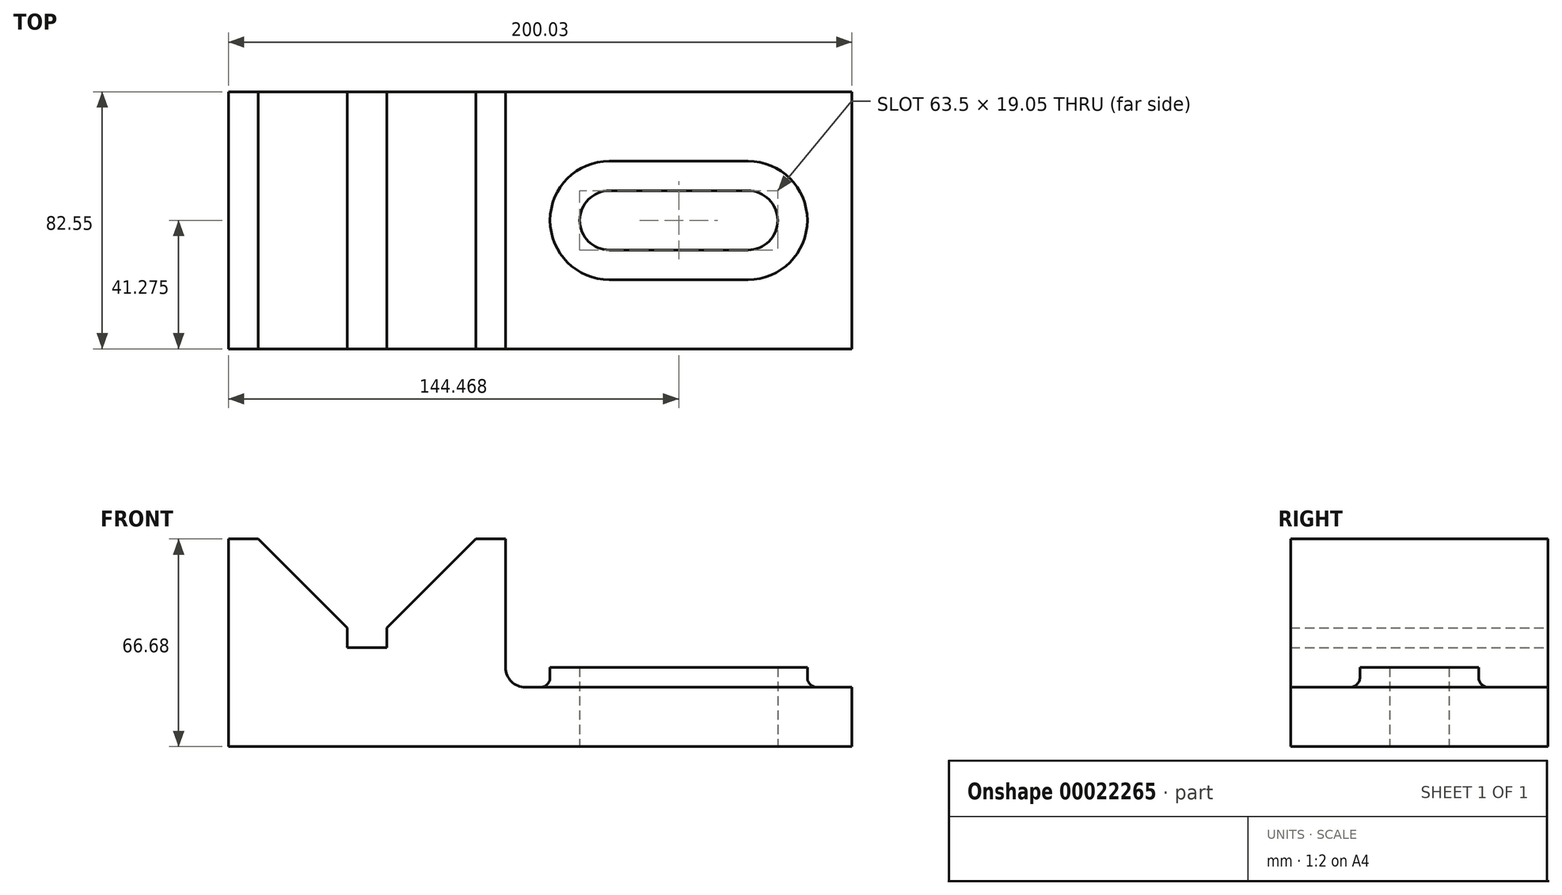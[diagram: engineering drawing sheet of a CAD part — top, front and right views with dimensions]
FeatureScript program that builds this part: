
annotation { "Feature Type Name" : "Feature", "Feature Type Description" : "" }
export const myFeature = defineFeature(function(context is Context, id is Id, definition is map)
    precondition{}
    {
        {
            var Q0;
            Q0=qCreatedBy(makeId("Front.planeOp"),FACE);
            var sketch = newSketch(context, id + "F0", { "sketchPlane" : qUnion([Q0])});
            skLineSegment(sketch, "E0.bottom", {"start": v(0, 0) * mm, "end": v(-200.03, 0) * mm});
            skLineSegment(sketch, "E0.top", {"start": v(0, 66.68) * mm, "end": v(-200.03, 66.68) * mm});
            skLineSegment(sketch, "E0.left", {"start": v(0, 0) * mm, "end": v(0, 66.68) * mm});
            skLineSegment(sketch, "E0.right", {"start": v(-200.03, 0) * mm, "end": v(-200.03, 66.67) * mm});
            skLineSegment(sketch, "E1", {"start": v(-190.5, 66.67) * mm, "end": v(-161.92, 38.1) * mm});
            skLineSegment(sketch, "E2", {"start": v(-161.92, 38.1) * mm, "end": v(-161.92, 31.75) * mm});
            skLineSegment(sketch, "E3", {"start": v(-161.92, 31.75) * mm, "end": v(-149.22, 31.75) * mm});
            skLineSegment(sketch, "E4", {"start": v(-149.22, 31.75) * mm, "end": v(-149.22, 38.1) * mm});
            skLineSegment(sketch, "E5", {"start": v(-149.22, 38.1) * mm, "end": v(-120.65, 66.67) * mm});
            skLineSegment(sketch, "E6", {"start": v(-111.12, 66.67) * mm, "end": v(-111.12, 0) * mm});
            skLineSegment(sketch, "E7", {"start": v(-161.92, 38.1) * mm, "end": v(-186.95, 38.1) * mm, "construction": true});
            skLineSegment(sketch, "E8", {"start": v(-149.22, 38.1) * mm, "end": v(-132.28, 38.1) * mm, "construction": true});
            skLineSegment(sketch, "E9", {"start": v(-111.12, 19.05) * mm, "end": v(0, 19.05) * mm});
            skSolve(sketch);
        }
        {
            var Q0;
            {var subQ0=sQuery(id+"F0.wireOp",EDGE,"E9");Q0=makeQuery(id+"F0.imprint","IMPRINT",FACE,{"disambiguationData":[TD([[makeQuery(id+"F0.imprint","IMPRINT",EDGE,{"derivedFrom":subQ0}),-1.0]])]});}
            var Q1;
            {var subQ8=sQuery(id+"F0.wireOp",EDGE,"E0.right");Q1=makeQuery(id+"F0.imprint","IMPRINT",FACE,{"disambiguationData":[TD([[makeQuery(id+"F0.imprint","IMPRINT",EDGE,{"derivedFrom":subQ8}),-1.0]])]});}
            extrude(context, id + "F1", {"entities" : qUnion([Q0, Q1]), "depth" : 82.55 * mm});
        }
        {
            var Q0;
            Q0=makeQuery(id+"F1.opExtrude","SWEPT_FACE",FACE,{"disambiguationData":[OSD([sQuery(id+"F0.wireOp",EDGE,"E9")])]});
            var sketch = newSketch(context, id + "F2", { "sketchPlane" : qUnion([Q0])});
            skLineSegment(sketch, "E10", {"start": v(0, -41.28) * mm, "end": v(-111.12, -41.28) * mm, "construction": true});
            skLineSegment(sketch, "E11", {"start": v(-55.56, -41.28) * mm, "end": v(-55.56, -2.33) * mm, "construction": true});
            skLineSegment(sketch, "E12", {"start": v(-55.56, -41.28) * mm, "end": v(-55.56, -63.94) * mm, "construction": true});
            skCircle(sketch, "E13", {"center": v(-77.79, -41.28) * mm, "radius": 9.53 * mm});
            skCircle(sketch, "E14", {"center": v(-33.34, -41.28) * mm, "radius": 9.53 * mm});
            skLineSegment(sketch, "E15", {"start": v(-77.79, -31.75) * mm, "end": v(-33.34, -31.75) * mm});
            skLineSegment(sketch, "E16", {"start": v(-77.79, -50.8) * mm, "end": v(-33.34, -50.8) * mm});
            skCircle(sketch, "E17", {"center": v(-33.34, -41.28) * mm, "radius": 19.05 * mm});
            skCircle(sketch, "E18", {"center": v(-77.79, -41.28) * mm, "radius": 19.05 * mm});
            skLineSegment(sketch, "E19", {"start": v(-77.79, -22.23) * mm, "end": v(-33.34, -22.23) * mm});
            skLineSegment(sketch, "E20", {"start": v(-77.79, -60.33) * mm, "end": v(-33.34, -60.33) * mm});
            skSolve(sketch);
        }
        {
            var Q0;
            Q0 = qSketchRegion(id + "F2", true);
            extrude(context, id + "F3", {"entities" : qUnion([Q0]), "operationType" : NewBodyOperationType.ADD, "depth" : 6.35 * mm});
        }
        {
            var Q0;
            Q0=makeQuery(id+"F3.boolean.opBoolean","SPLIT",FACE,{"disambiguationData":[TD([makeQuery(id+"F3.opExtrude","SWEPT_FACE",FACE,{"disambiguationData":[OSD([sQuery(id+"F2.wireOp",EDGE,"E13")])]})])],"derivedFrom":makeQuery(id+"F1.opExtrude","SWEPT_FACE",FACE,{"disambiguationData":[OSD([sQuery(id+"F0.wireOp",EDGE,"E9")])]})});
            extrude(context, id + "F4", {"entities" : qUnion([Q0]), "operationType" : NewBodyOperationType.REMOVE, "endBound" : BoundingType.THROUGH_ALL, "oppositeDirection" : true, "depth" : 25.4 * mm});
        }
        {
            var Q0;
            Q0=makeQuery(id+"F1.opExtrude","SWEPT_EDGE",EDGE,{"disambiguationData":[OSD([sQuery(id+"F0.wireOp",EDGE,"E6"),sQuery(id+"F0.wireOp",EDGE,"E9")])]});
            fillet(context, id + "F5", {"entities" : qUnion([Q0]), "radius" : 6.35 * mm, "tangentPropagation" : true, "allowEdgeOverflow" : false});
        }
        {
            var Q0;
            Q0=makeQuery(id+"F3.opExtrude","CAP_EDGE",EDGE,{"disambiguationData":[OSD([sQuery(id+"F2.wireOp",EDGE,"E20")])],"isStart":true});
            fillet(context, id + "F6", {"entities" : qUnion([Q0]), "radius" : 3.17 * mm, "tangentPropagation" : true, "allowEdgeOverflow" : false});
        }
    });
